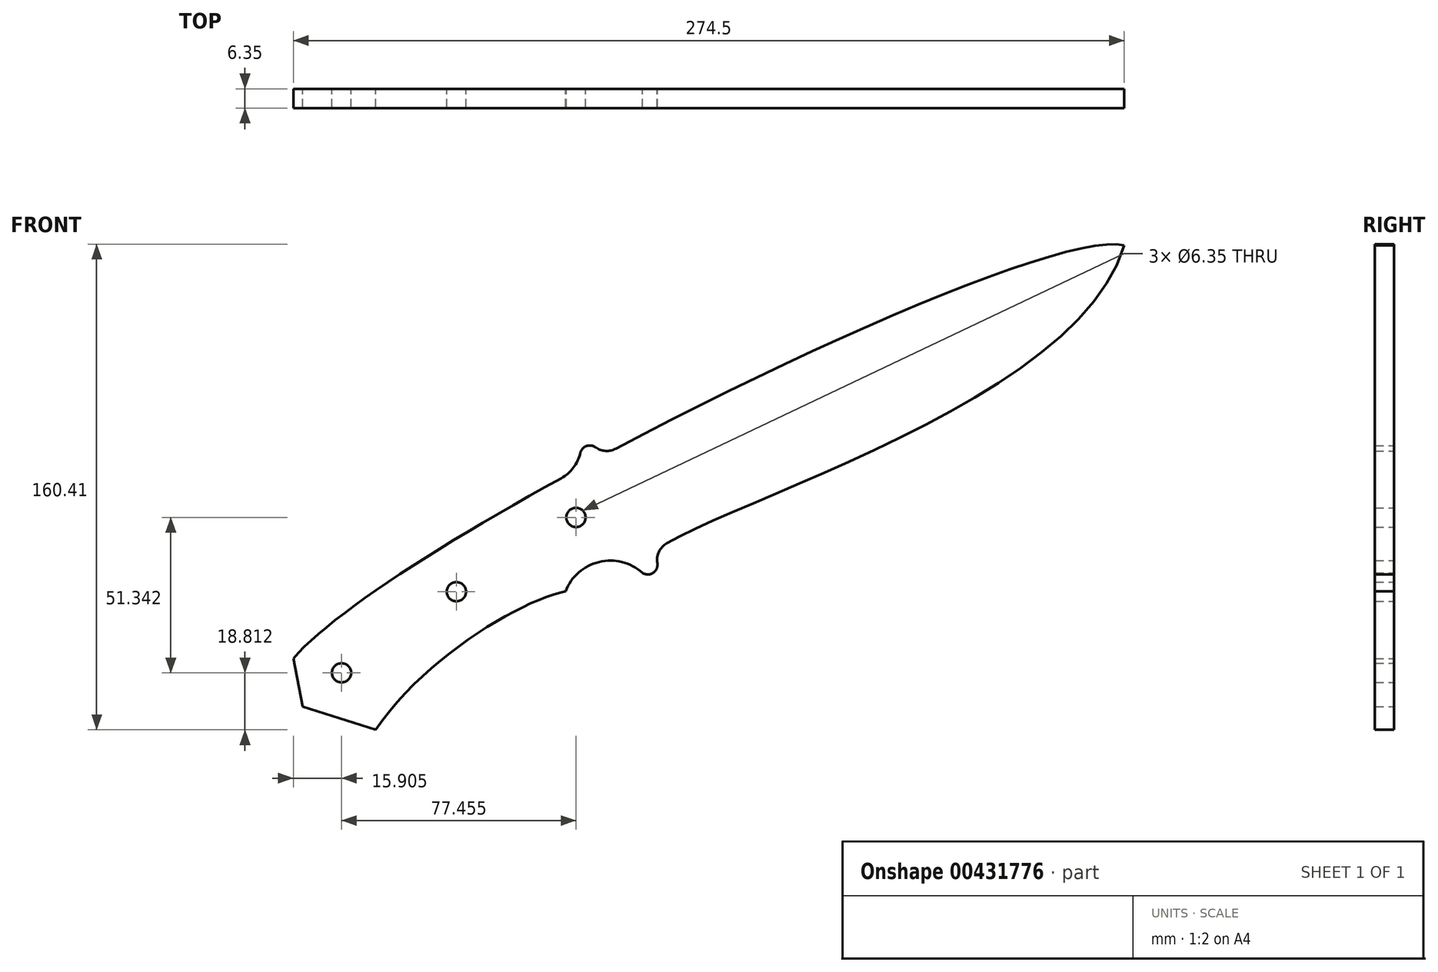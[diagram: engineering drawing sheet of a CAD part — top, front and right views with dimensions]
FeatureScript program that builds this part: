
annotation { "Feature Type Name" : "Feature", "Feature Type Description" : "" }
export const myFeature = defineFeature(function(context is Context, id is Id, definition is map)
    precondition{}
    {
        {
            var Q0;
            Q0=qCreatedBy(makeId("Front.planeOp"),FACE);
            var sketch = newSketch(context, id + "F0", { "sketchPlane" : qUnion([Q0])});
            skFitSpline(sketch, "E0", {"points": [v(-114.45, -80.77) * mm, v(157.02, 71.27) * mm], "startDerivative": vector(184.4, 137.85) * mm, "endDerivative": vector(512.76, 231.03) * mm});
            skSolve(sketch);
        }
        {
            var Q0;
            Q0=qCreatedBy(makeId("Front.planeOp"),FACE);
            var sketch = newSketch(context, id + "F1", { "sketchPlane" : qUnion([Q0])});
            skFitSpline(sketch, "E1", {"points": [v(157.2, 71.41) * mm, v(-117.3, -65.04) * mm], "startDerivative": vector(-86.44, 23.87) * mm, "endDerivative": vector(-99.76, -117.87) * mm});
            skFitSpline(sketch, "E2", {"points": [v(-90.07, -88.57) * mm, v(-27.4, -42.83) * mm], "startDerivative": vector(49.3, 73.03) * mm, "endDerivative": vector(42.91, 8.61) * mm});
            skArc(sketch, "E3", {"start": v(-2.02, -36.7) * mm, "mid": v(-16.3, -33.15) * mm, "end": v(-27.4, -42.83) * mm});
            skFitSpline(sketch, "E4", {"points": [v(3.13, -28.75) * mm, v(157.2, 71.41) * mm], "startDerivative": vector(75.83, 50.28) * mm, "endDerivative": vector(46.15, 154.65) * mm});
            skArc(sketch, "E5", {"start": v(-17.45, 4.73) * mm, "mid": v(-20.5, 5.13) * mm, "end": v(-22.54, 2.81) * mm});
            skArc(sketch, "E6", {"start": v(-2, -36.7) * mm, "mid": v(1.52, -36.78) * mm, "end": v(2.95, -33.56) * mm});
            skLineSegment(sketch, "E7", {"start": v(-2.02, -36.7) * mm, "end": v(-2, -36.7) * mm});
            skArc(sketch, "E8.filletArc", {"start": v(6.06, -26.96) * mm, "mid": v(3.46, -29.77) * mm, "end": v(2.95, -33.56) * mm});
            skFitSpline(sketch, "E9.trimOffspring", {"points": [v(157.2, 71.41) * mm, v(-117.3, -65.04) * mm], "startDerivative": vector(-86.44, 23.87) * mm, "endDerivative": vector(-99.76, -117.87) * mm});
            skPoint(sketch, "E10.visualSharp", {"position": v(-16.14, 1.43) * mm});
            skArc(sketch, "E10.filletArc", {"start": v(-17.45, 4.73) * mm, "mid": v(-14.18, 3.56) * mm, "end": v(-10.78, 4.29) * mm});
            skPoint(sketch, "E11.visualSharp", {"position": v(-20.58, -0.96) * mm});
            skArc(sketch, "E12.filletArc", {"start": v(-28.78, -5.44) * mm, "mid": v(-24.78, -1.98) * mm, "end": v(-22.54, 2.81) * mm});
            skLineSegment(sketch, "E13", {"start": v(-117.3, -65.04) * mm, "end": v(-114.26, -80.9) * mm});
            skLineSegment(sketch, "E14", {"start": v(-114.26, -80.9) * mm, "end": v(-90.07, -88.57) * mm});
            skSolve(sketch);
        }
        {
            var Q0;
            Q0=qSketchRegion(id+"F1",true);
            extrude(context, id + "F2", {"entities" : qUnion([Q0]), "depth" : 6.35 * mm});
        }
        {
            var Q0;
            Q0=qCreatedBy(makeId("Front.planeOp"),FACE);
            var sketch = newSketch(context, id + "F3", { "sketchPlane" : qUnion([Q0])});
            skCircle(sketch, "E15", {"center": v(-101.38, -69.76) * mm, "radius": 3.18 * mm});
            skCircle(sketch, "E16", {"center": v(-63.45, -42.96) * mm, "radius": 3.18 * mm});
            skCircle(sketch, "E17", {"center": v(-23.93, -18.42) * mm, "radius": 3.18 * mm});
            skSolve(sketch);
        }
        {
            var Q0;
            Q0=qSketchRegion(id+"F3",true);
            var Q1;
            Q1=makeQuery(id+"F2.opExtrude","CAP_FACE",FACE,{"disambiguationData":[OSD([sQuery(id+"F1.wireOp",EDGE,"E1"),sQuery(id+"F1.wireOp",EDGE,"E2"),sQuery(id+"F1.wireOp",EDGE,"E3"),sQuery(id+"F1.wireOp",EDGE,"E4"),sQuery(id+"F1.wireOp",EDGE,"E5"),sQuery(id+"F1.wireOp",EDGE,"E6"),sQuery(id+"F1.wireOp",EDGE,"E7"),sQuery(id+"F1.wireOp",EDGE,"E8.filletArc"),sQuery(id+"F1.wireOp",EDGE,"E9.trimOffspring"),sQuery(id+"F1.wireOp",EDGE,"E10.filletArc"),sQuery(id+"F1.wireOp",EDGE,"E12.filletArc"),sQuery(id+"F1.wireOp",EDGE,"E13"),sQuery(id+"F1.wireOp",EDGE,"E14")])],"isStart":false});
            extrude(context, id + "F4", {"entities" : qUnion([Q0, Q1]), "operationType" : NewBodyOperationType.REMOVE, "endBound" : BoundingType.THROUGH_ALL, "depth" : 25.4 * mm});
        }
    });
